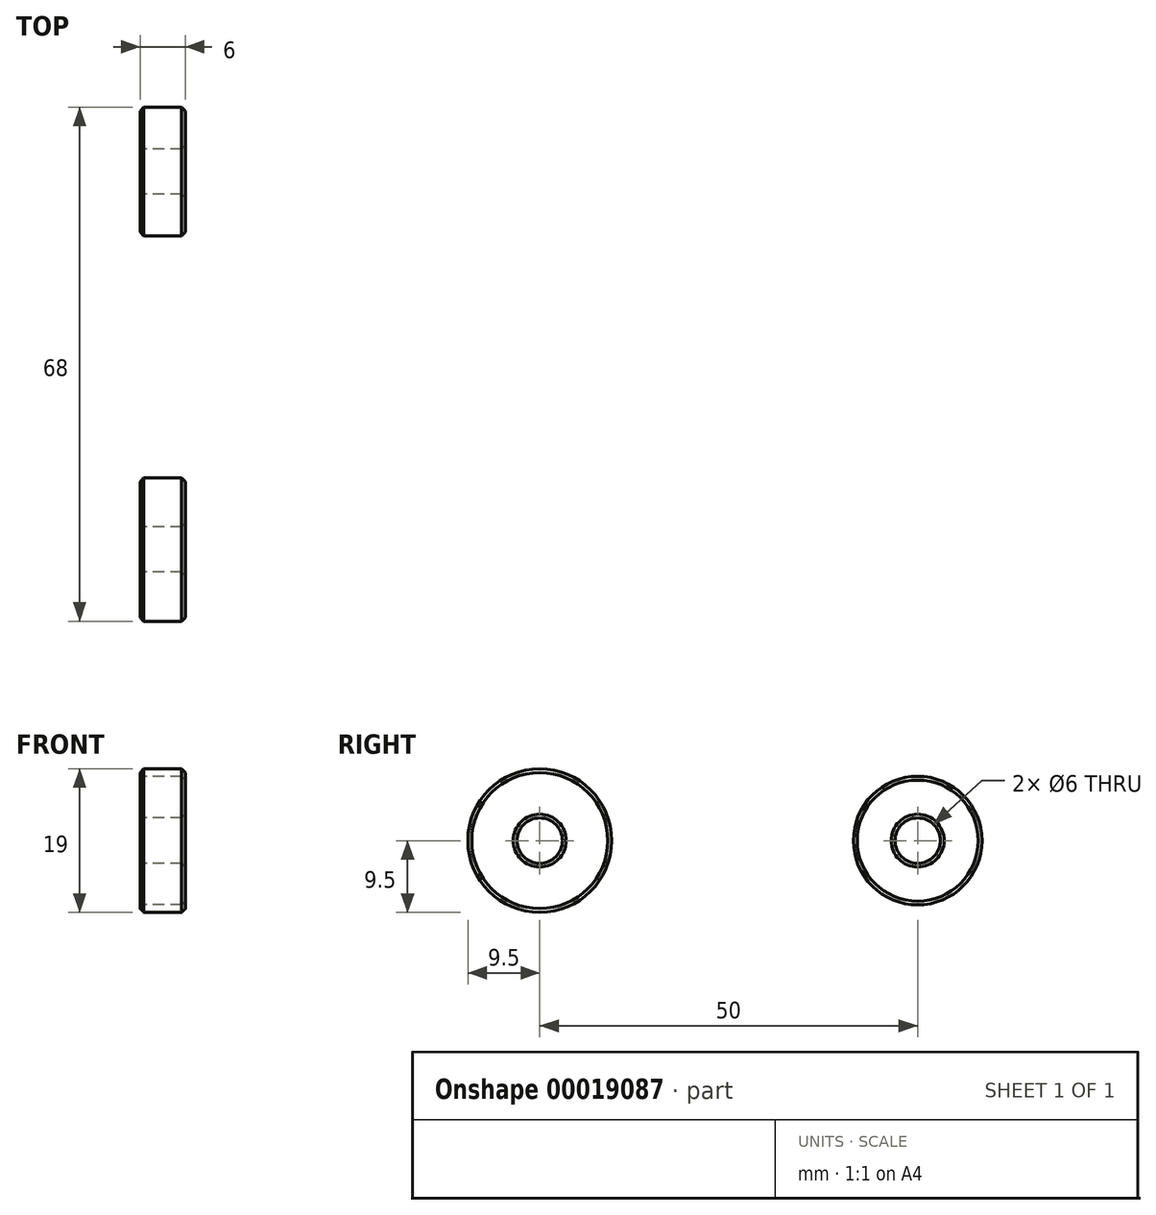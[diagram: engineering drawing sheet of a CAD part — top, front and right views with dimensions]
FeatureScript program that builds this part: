
annotation { "Feature Type Name" : "Feature", "Feature Type Description" : "" }
export const myFeature = defineFeature(function(context is Context, id is Id, definition is map)
    precondition{}
    {
        {
            var Q0;
            Q0=qCreatedBy(makeId("Right.planeOp"),FACE);
            var sketch = newSketch(context, id + "F0", { "sketchPlane" : qUnion([Q0])});
            skCircle(sketch, "E0", {"center": v(0, 0) * mm, "radius": 3 * mm});
            skCircle(sketch, "E1", {"center": v(0, 0) * mm, "radius": 9.5 * mm});
            skLineSegment(sketch, "E2", {"start": v(0, 0) * mm, "end": v(50, 0) * mm, "construction": true});
            skCircle(sketch, "E3", {"center": v(50, 0) * mm, "radius": 8.5 * mm});
            skCircle(sketch, "E4", {"center": v(50, 0) * mm, "radius": 3 * mm});
            skSolve(sketch);
        }
        {
            var Q0;
            Q0=qSketchRegion(id+"F0",true);
            extrude(context, id + "F1", {"entities" : qUnion([Q0]), "depth" : 6 * mm});
        }
        {
            var Q0;
            Q0=makeQuery(id+"F1.opExtrude","CAP_EDGE",EDGE,{"disambiguationData":[OSD([sQuery(id+"F0.wireOp",EDGE,"E1")])],"isStart":false});
            var Q1;
            Q1=makeQuery(id+"F1.opExtrude","CAP_EDGE",EDGE,{"disambiguationData":[OSD([sQuery(id+"F0.wireOp",EDGE,"E1")])],"isStart":true});
            var Q2;
            Q2=makeQuery(id+"F1.opExtrude","CAP_EDGE",EDGE,{"disambiguationData":[OSD([sQuery(id+"F0.wireOp",EDGE,"E0")])],"isStart":true});
            var Q3;
            Q3=makeQuery(id+"F1.opExtrude","CAP_EDGE",EDGE,{"disambiguationData":[OSD([sQuery(id+"F0.wireOp",EDGE,"E0")])],"isStart":false});
            var Q4;
            Q4=makeQuery(id+"F1.opExtrude","CAP_EDGE",EDGE,{"disambiguationData":[OSD([sQuery(id+"F0.wireOp",EDGE,"E4")])],"isStart":false});
            var Q5;
            Q5=makeQuery(id+"F1.opExtrude","CAP_EDGE",EDGE,{"disambiguationData":[OSD([sQuery(id+"F0.wireOp",EDGE,"E3")])],"isStart":false});
            var Q6;
            Q6=makeQuery(id+"F1.opExtrude","CAP_EDGE",EDGE,{"disambiguationData":[OSD([sQuery(id+"F0.wireOp",EDGE,"E3")])],"isStart":true});
            var Q7;
            Q7=makeQuery(id+"F1.opExtrude","CAP_EDGE",EDGE,{"disambiguationData":[OSD([sQuery(id+"F0.wireOp",EDGE,"E4")])],"isStart":true});
            chamfer(context, id + "F2", {"entities" : qUnion([Q0, Q1, Q2, Q3, Q4, Q5, Q6, Q7]), "width" : 0.5 * mm, "tangentPropagation" : true});
        }
    });
